# Revit family: Domotics-DomesticRanges-GEWISS-CHORUS_COMMAND-PUSH-BUTTON_DOUBLE_1M
name_source: partatom
category: Apparecchi elettrici
revit_build: Autodesk Revit 2016 (Build: 20161004_0715(x64)
units: mm (PartAtom-declared; Revit-internal decimal feet)

## family parameters
Condiviso = Sì
Host = Superficie
Mantenere orientamento annotazione = Sì
Numero OmniClass = 23.80.50.11.14
Punto di calcolo locali = Sì
Quota connettore circolare = Usa diametro
Taglio con vuoti quando caricato = Sì
Tipo di parte = Normale
Titolo OmniClass = Switches

## types (12) — shared parameters
Bidimensionale = bidimensionale pulsanti doppi 1m : spia
Breaking capacity: = 1.25 In (200 position changes)
Catalogue = DOMOTICS
Catalogue Range = CHORUS - DOMESTIC RANGE
Category = Push-button
Electrocod = 0130
Glow Wire Test = 850°C
IDF = 2e8034d1-03a1-4e93-8a43-b73501fad585
IDT = e94f411e-52af-40ad-8ae0-9443e08576e5
Immagine tipo = GW14144.jpg
Insulation resistance = > 5 MOhm
Larghezza pulsante = 23 mm  [stored 0.0754593 ft]
No. Chorus modules = 1
Number of poles = 1P
Produttore = GEWISS S.p.A.
Prolonged operation (no.of position changes) = 40.000 at In 250 V ac cosÃ˜=0,6
Prospetto di default = 1219 mm
Resistance at test voltage = 2000 V at 50 Hz for 1 minute
SEO = Push button
Simbolo_ = SIMBOLO PULSANTI : LUM
Standard; = EN 60669-1
Technical sheet = https://www.gewiss.com
Terminal grip on cable traction = > 50 N
Terminal tightening capacity flexible cables (mm2) = min. 0,75 - max. 2x4
Terminal tightening capacity rigid cables (mm2) = min. 0,5 - max. 2x2,5
Thermo-pressure with ball = 125
Tipo_ = CHORUS PULSANTI DOPPI 1M_BASE : GW14144 - Titanio
URL = https://www.gewiss.com
Version file RFA = 19.0
Voltage = 250 V ac
Voltage: = 250 V ac
Wiring terminals = With screw

## per-type parameters (varying)
| type | Button key | Colour | Description: | Descrizione | EAN code | Modello | Type |
| GW12143 - Black | Red diffuser | Black | 1P NO - 16A illuminable | P-BUTTON 1M 1P NO 16A RED LAMP, BLACK | 8011564269620 | GW12143 | Red diffuser |
| GW12142 - Black | Green diffuser | Black | 1P NO - 16A illuminable | P-BUTTON 1M 1P NO 16A GREEN LAMP, BLACK | 8011564269613 | GW12142 | Green diffuser |
| GW10144 - White | Opal diffuser | White | 1P NO - 16A illuminable | P-BUTTON 1M 1P NO 16A TRANSP LAMP, WHITE | 8011564260825 | GW10144 | Opal diffuser |
| GW12144 - Black | Opal diffuser | Black | 1P NO - 16A illuminable | P-BUTTON 1M 1P NO 16A TRANSP LAMP, BLACK | 8011564269637 | GW12144 | Opal diffuser |
| GW14142 - Titanium | Green diffuser | Titanium | 1P NO - 16A illuminable | P-BUTTON 1M 1P NO 16A GRN LAMP, TITANIUM | 8011564265943 | GW14142 | Green diffuser |
| GW14144 - Titanium | Opal diffuser | Titanium | 1P NO - 16A illuminable | P-BUTTON 1M 1P NO 16A TRP LAMP, TITANIUM | 8011564265967 | GW14144 | Opal diffuser |
| GW10142 - White | Green diffuser | White | 1P NO - 16A illuminable | P-BUTTON, 1M 1P NO 16A GREEN LAMP, WHITE | 8011564260801 | GW10142 | Green diffuser |
| GW10143 - White | Red diffuser | White | 1P NO - 16A illuminable | P-BUTTON, 1M 1P NO 16A RED LAMP, WHITE | 8011564260818 | GW10143 | Red diffuser |
| GW14141 - Titanium | Double | Titanium | 1P NO+NO - 16 A | PUSH-BUTTON 1M DOUBLE NO 16A TITANIUM | 8011564265936 | GW14141 | Double |
| GW10141 - White | Double | White | 1P NO+NO - 16 A | PUSH-BUTTON, 1M DOUBLE NO 16A WHITE | 8011564261853 | GW10141 | Double |
| GW14143 - Titanium | Red diffuser | Titanium | 1P NO - 16A illuminable | P-BUTTON 1M 1P NO 16A RED LAMP, TITANIUM | 8011564265950 | GW14143 | Red diffuser |
| GW12141 - Black | Double | Black | 1P NO+NO - 16 A | PUSH-BUTTON 1M DOUBLE NO 16A BLACK | 8011564269606 | GW12141 | Double |

note: source unit labels omitted for Thermo-pressure with ball — the stored unit's dimension contradicts the parameter name (converter mislabeling)

note: [stored X ft] marks values corroborated as IEEE doubles in the binary element streams (Revit-internal decimal feet)

## geometry (parser evidence)
native form markers: Sweep x1
no freeform markers — native parametric forms only
